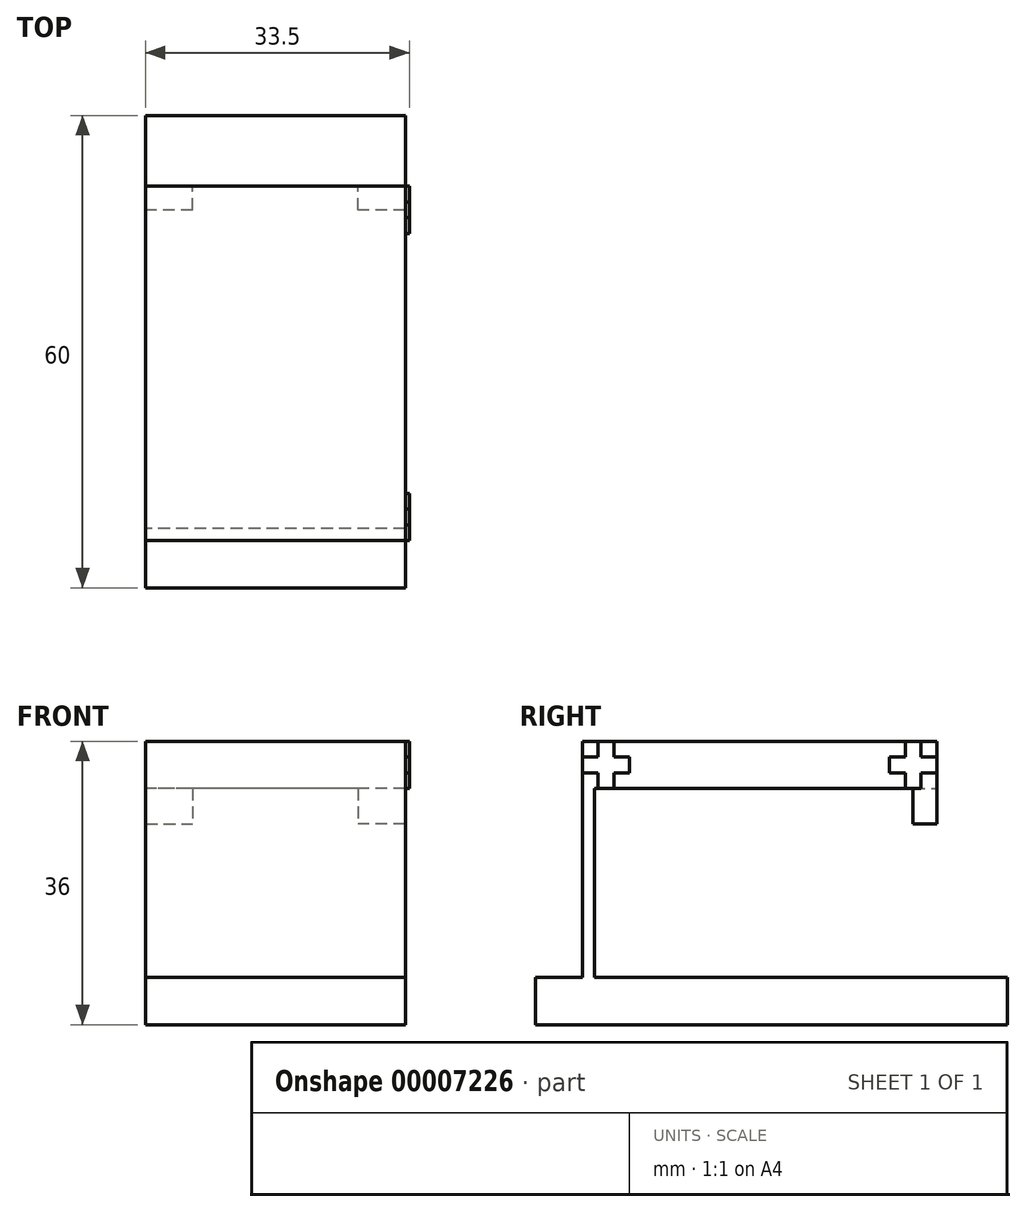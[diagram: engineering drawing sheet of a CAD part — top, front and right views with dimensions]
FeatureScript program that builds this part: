
annotation { "Feature Type Name" : "Feature", "Feature Type Description" : "" }
export const myFeature = defineFeature(function(context is Context, id is Id, definition is map)
    precondition{}
    {
        {
            var Q0;
            Q0=qCreatedBy(makeId("Right.planeOp"),FACE);
            var sketch = newSketch(context, id + "F0", { "sketchPlane" : qUnion([Q0])});
            skLineSegment(sketch, "E0", {"start": v(1.5, 30) * mm, "end": v(42, 30) * mm});
            skLineSegment(sketch, "E1", {"start": v(45, 30) * mm, "end": v(45, 36) * mm});
            skLineSegment(sketch, "E2", {"start": v(45, 36) * mm, "end": v(0, 36) * mm});
            skLineSegment(sketch, "E3", {"start": v(0, 36) * mm, "end": v(0, 6) * mm});
            skLineSegment(sketch, "E4", {"start": v(0, 0) * mm, "end": v(54, 0) * mm});
            skLineSegment(sketch, "E5", {"start": v(1.5, 30) * mm, "end": v(1.5, 6) * mm});
            skLineSegment(sketch, "E6", {"start": v(1.5, 6) * mm, "end": v(54, 6) * mm});
            skLineSegment(sketch, "E7", {"start": v(54, 6) * mm, "end": v(54, 0) * mm});
            skPoint(sketch, "E8", {"position": v(42, 30) * mm});
            skPoint(sketch, "E9", {"position": v(0, 30) * mm});
            skPoint(sketch, "E10", {"position": v(0, 6) * mm});
            skLineSegment(sketch, "E11", {"start": v(0, 6) * mm, "end": v(-6, 6) * mm});
            skLineSegment(sketch, "E12", {"start": v(-6, 6) * mm, "end": v(-6, 0) * mm});
            skLineSegment(sketch, "E13", {"start": v(-6, 0) * mm, "end": v(0, 0) * mm});
            skPoint(sketch, "E14.end.orphan", {"position": v(45, 22.38) * mm});
            skLineSegment(sketch, "E15", {"start": v(42, 30) * mm, "end": v(45, 30) * mm});
            skSolve(sketch);
        }
        {
            var Q0;
            Q0=qSketchRegion(id+"F0",true);
            extrude(context, id + "F1", {"entities" : qUnion([Q0]), "depth" : 33 * mm});
        }
        {
            var Q0;
            Q0=makeQuery(id+"F1.opExtrude","SWEPT_FACE",FACE,{"disambiguationData":[OSD([sQuery(id+"F0.wireOp",EDGE,"E1")])]});
            var sketch = newSketch(context, id + "F2", { "sketchPlane" : qUnion([Q0])});
            skLineSegment(sketch, "E16.bottom", {"start": v(-33, 30) * mm, "end": v(-27, 30) * mm});
            skLineSegment(sketch, "E16.top", {"start": v(-33, 25.5) * mm, "end": v(-27, 25.5) * mm});
            skLineSegment(sketch, "E16.left", {"start": v(-33, 30) * mm, "end": v(-33, 25.5) * mm});
            skLineSegment(sketch, "E16.right", {"start": v(-27, 30) * mm, "end": v(-27, 25.5) * mm});
            skLineSegment(sketch, "E17.bottom", {"start": v(0, 30) * mm, "end": v(-6, 30) * mm});
            skLineSegment(sketch, "E17.top", {"start": v(0, 25.5) * mm, "end": v(-6, 25.5) * mm});
            skLineSegment(sketch, "E17.left", {"start": v(0, 30) * mm, "end": v(0, 25.5) * mm});
            skLineSegment(sketch, "E17.right", {"start": v(-6, 30) * mm, "end": v(-6, 25.5) * mm});
            skLineSegment(sketch, "E18", {"start": v(-16.5, 30) * mm, "end": v(-16.5, 12.44) * mm, "construction": true});
            skSolve(sketch);
        }
        {
            var Q0;
            Q0=qSketchRegion(id+"F2",true);
            extrude(context, id + "F3", {"entities" : qUnion([Q0]), "oppositeDirection" : true, "depth" : 3 * mm});
        }
        {
            var Q0;
            Q0=makeQuery(id+"F1.opExtrude","SWEPT_BODY",BODY,{"disambiguationData":[OSD([sQuery(id+"F0.wireOp",EDGE,"E0"),sQuery(id+"F0.wireOp",EDGE,"E1"),sQuery(id+"F0.wireOp",EDGE,"E2"),sQuery(id+"F0.wireOp",EDGE,"E3"),sQuery(id+"F0.wireOp",EDGE,"E4"),sQuery(id+"F0.wireOp",EDGE,"E5"),sQuery(id+"F0.wireOp",EDGE,"E6"),sQuery(id+"F0.wireOp",EDGE,"E7"),sQuery(id+"F0.wireOp",EDGE,"E11"),sQuery(id+"F0.wireOp",EDGE,"E12"),sQuery(id+"F0.wireOp",EDGE,"E13"),sQuery(id+"F0.wireOp",EDGE,"E15")])]});
            var Q1;
            Q1=makeQuery(id+"F6WPI06lxKIipIr_1.opExtrude","SWEPT_BODY",BODY,{"disambiguationData":[OSD([sQuery(id+"FRPDtzmPnAjLNcS_1.wireOp",EDGE,"9a1b587a-3da7-49af-bdb7-b956a9bc8941"),sQuery(id+"FRPDtzmPnAjLNcS_1.wireOp",EDGE,"bf295e85-8bde-4aab-a36f-4a9de244f566"),sQuery(id+"FRPDtzmPnAjLNcS_1.wireOp",EDGE,"8b9e3d9a-fcde-4b25-82a9-674ecc5d6e69"),sQuery(id+"FRPDtzmPnAjLNcS_1.wireOp",EDGE,"b9fa87d3-3e8d-4bad-91c5-1e4c7279e79b")])]});
            var Q2;
            Q2=makeQuery(id+"F3.opExtrude","SWEPT_BODY",BODY,{"disambiguationData":[OSD([sQuery(id+"F2.wireOp",EDGE,"E17.bottom"),sQuery(id+"F2.wireOp",EDGE,"E17.top"),sQuery(id+"F2.wireOp",EDGE,"E17.left"),sQuery(id+"F2.wireOp",EDGE,"E17.right")])]});
            var Q3;
            Q3=makeQuery(id+"F3.opExtrude","SWEPT_BODY",BODY,{"disambiguationData":[OSD([sQuery(id+"F2.wireOp",EDGE,"E16.bottom"),sQuery(id+"F2.wireOp",EDGE,"E16.top"),sQuery(id+"F2.wireOp",EDGE,"E16.left"),sQuery(id+"F2.wireOp",EDGE,"E16.right")])]});
            var Q4;
            Q4=makeQuery(id+"FJlxdcFNMPX0Xzt_2.opExtrude","SWEPT_BODY",BODY,{"disambiguationData":[OSD([sQuery(id+"FfzIguvbrS8OUP2_2.wireOp",EDGE,"078e5c98-56e0-428d-afe6-236eedcddf04"),sQuery(id+"FfzIguvbrS8OUP2_2.wireOp",EDGE,"975a3c9d-05ae-4e77-b171-0c8f3cf14303"),sQuery(id+"FfzIguvbrS8OUP2_2.wireOp",EDGE,"288a9a5e-099b-47e2-b2ce-dfeccd1bad30"),sQuery(id+"FfzIguvbrS8OUP2_2.wireOp",EDGE,"572c8bbc-5c0e-4594-9375-c5b2b3b89553")])]});
            booleanBodies(context, id + "F4", {"operationType" : BooleanOperationType.UNION, "tools" : qUnion([Q0, Q1, Q2, Q3, Q4])});
        }
        {
            var Q0;
            Q0=makeQuery(id+"F4.opBoolean","MERGE",FACE,{"derivedFrom":[makeQuery(id+"F1.opExtrude","CAP_FACE",FACE,{"disambiguationData":[OSD([sQuery(id+"F0.wireOp",EDGE,"E0"),sQuery(id+"F0.wireOp",EDGE,"E1"),sQuery(id+"F0.wireOp",EDGE,"E2"),sQuery(id+"F0.wireOp",EDGE,"E3"),sQuery(id+"F0.wireOp",EDGE,"E4"),sQuery(id+"F0.wireOp",EDGE,"E5"),sQuery(id+"F0.wireOp",EDGE,"E6"),sQuery(id+"F0.wireOp",EDGE,"E7"),sQuery(id+"F0.wireOp",EDGE,"E11"),sQuery(id+"F0.wireOp",EDGE,"E12"),sQuery(id+"F0.wireOp",EDGE,"E13"),sQuery(id+"F0.wireOp",EDGE,"E15")])],"isStart":false}),makeQuery(id+"F3.opExtrude","SWEPT_FACE",FACE,{"disambiguationData":[OSD([sQuery(id+"F2.wireOp",EDGE,"E16.left")])]})]});
            var sketch = newSketch(context, id + "F5", { "sketchPlane" : qUnion([Q0])});
            skLineSegment(sketch, "E19", {"start": v(22.5, 36) * mm, "end": v(22.5, 30) * mm, "construction": true});
            skLineSegment(sketch, "E20.bottom", {"start": v(0, 34) * mm, "end": v(2, 34) * mm});
            skLineSegment(sketch, "E20.top", {"start": v(0, 32) * mm, "end": v(2, 32) * mm});
            skLineSegment(sketch, "E20.left", {"start": v(0, 34) * mm, "end": v(0, 32) * mm});
            skLineSegment(sketch, "E20.right", {"start": v(6, 34) * mm, "end": v(6, 32) * mm});
            skLineSegment(sketch, "E21.bottom", {"start": v(39, 34) * mm, "end": v(41, 34) * mm});
            skLineSegment(sketch, "E21.top", {"start": v(39, 32) * mm, "end": v(41, 32) * mm});
            skLineSegment(sketch, "E21.left", {"start": v(39, 34) * mm, "end": v(39, 32) * mm});
            skLineSegment(sketch, "E21.right", {"start": v(45, 34) * mm, "end": v(45, 32) * mm});
            skLineSegment(sketch, "E22.bottom", {"start": v(2, 36) * mm, "end": v(4, 36) * mm});
            skLineSegment(sketch, "E22.top", {"start": v(2, 30) * mm, "end": v(4, 30) * mm});
            skLineSegment(sketch, "E22.left", {"start": v(2, 36) * mm, "end": v(2, 34) * mm});
            skLineSegment(sketch, "E22.right", {"start": v(4, 36) * mm, "end": v(4, 34) * mm});
            skLineSegment(sketch, "E23.bottom", {"start": v(41, 36) * mm, "end": v(43, 36) * mm});
            skLineSegment(sketch, "E23.top", {"start": v(41, 30) * mm, "end": v(43, 30) * mm});
            skLineSegment(sketch, "E23.left", {"start": v(41, 36) * mm, "end": v(41, 34) * mm});
            skLineSegment(sketch, "E23.right", {"start": v(43, 36) * mm, "end": v(43, 34) * mm});
            skPoint(sketch, "E24", {"position": v(2, 34) * mm});
            skPoint(sketch, "E25", {"position": v(4, 34) * mm});
            skPoint(sketch, "E26", {"position": v(4, 32) * mm});
            skPoint(sketch, "E27", {"position": v(2, 32) * mm});
            skPoint(sketch, "E28", {"position": v(41, 34) * mm});
            skPoint(sketch, "E29", {"position": v(43, 34) * mm});
            skPoint(sketch, "E30", {"position": v(43, 32) * mm});
            skPoint(sketch, "E31", {"position": v(41, 32) * mm});
            skLineSegment(sketch, "E32.trimOffspring", {"start": v(4, 32) * mm, "end": v(4, 30) * mm});
            skLineSegment(sketch, "E33.trimOffspring", {"start": v(4, 34) * mm, "end": v(6, 34) * mm});
            skLineSegment(sketch, "E34.trimOffspring", {"start": v(2, 32) * mm, "end": v(2, 30) * mm});
            skLineSegment(sketch, "E35.trimOffspring", {"start": v(4, 32) * mm, "end": v(6, 32) * mm});
            skLineSegment(sketch, "E36.trimOffspring", {"start": v(43, 34) * mm, "end": v(45, 34) * mm});
            skLineSegment(sketch, "E37.trimOffspring", {"start": v(41, 32) * mm, "end": v(41, 30) * mm});
            skLineSegment(sketch, "E38.trimOffspring", {"start": v(43, 32) * mm, "end": v(45, 32) * mm});
            skLineSegment(sketch, "E39.trimOffspring", {"start": v(43, 32) * mm, "end": v(43, 30) * mm});
            skSolve(sketch);
        }
        {
            var Q0;
            Q0=qSketchRegion(id+"F5",true);
            extrude(context, id + "F6", {"entities" : qUnion([Q0]), "depth" : 0.5 * mm});
        }
    });
